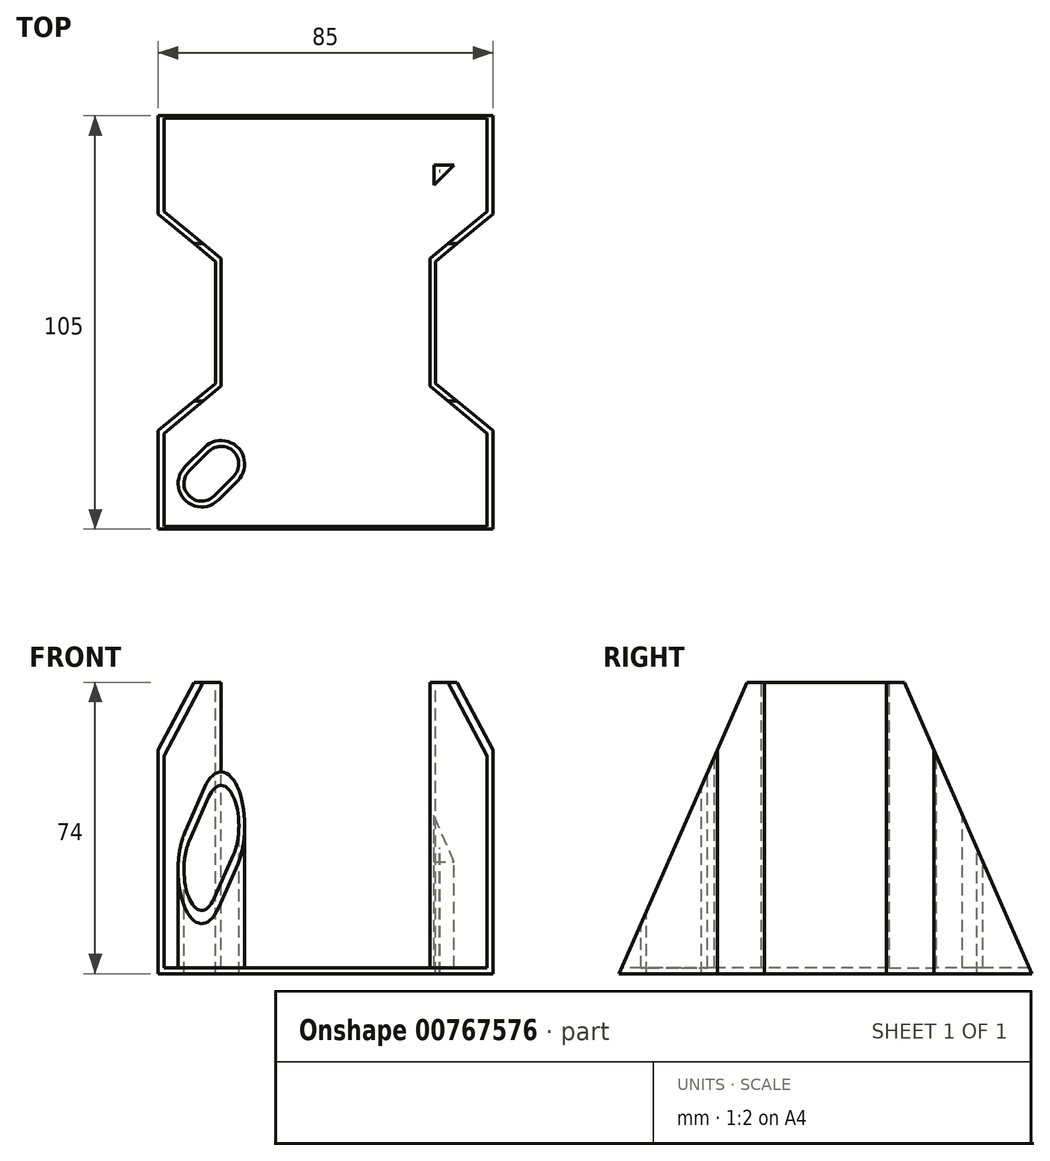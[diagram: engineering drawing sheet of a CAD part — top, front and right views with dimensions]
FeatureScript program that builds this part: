
annotation { "Feature Type Name" : "Feature", "Feature Type Description" : "" }
export const myFeature = defineFeature(function(context is Context, id is Id, definition is map)
    precondition{}
    {
        {
            var Q0;
            Q0=qCreatedBy(makeId("Top.planeOp"),FACE);
            var sketch = newSketch(context, id + "F0", { "sketchPlane" : qUnion([Q0])});
            skLineSegment(sketch, "E0.bottom", {"start": v(42.5, 52.5) * mm, "end": v(-42.5, 52.5) * mm});
            skLineSegment(sketch, "E0.top", {"start": v(42.5, -52.5) * mm, "end": v(-42.5, -52.5) * mm});
            skLineSegment(sketch, "E0.right", {"start": v(-42.5, 52.5) * mm, "end": v(-42.5, 27.5) * mm});
            skPoint(sketch, "E0.middle", {"position": v(0, 0) * mm});
            skLineSegment(sketch, "E1", {"start": v(-28, 15.5) * mm, "end": v(-28, -15.5) * mm});
            skLineSegment(sketch, "E2", {"start": v(-28, -15.5) * mm, "end": v(-42.5, -27.5) * mm});
            skLineSegment(sketch, "E3", {"start": v(-28, 15.5) * mm, "end": v(-42.5, 27.5) * mm});
            skLineSegment(sketch, "E4.trimOffspring", {"start": v(-42.5, -27.5) * mm, "end": v(-42.5, -52.5) * mm});
            skLineSegment(sketch, "E5.MirrorCS", {"start": v(42.5, 52.5) * mm, "end": v(42.5, 27.5) * mm});
            skLineSegment(sketch, "E6.MirrorCS", {"start": v(28, 15.5) * mm, "end": v(42.5, 27.5) * mm});
            skLineSegment(sketch, "E7.MirrorCS", {"start": v(28, 15.5) * mm, "end": v(28, -15.5) * mm});
            skLineSegment(sketch, "E8.MirrorCS", {"start": v(28, -15.5) * mm, "end": v(42.5, -27.5) * mm});
            skLineSegment(sketch, "E9.MirrorCS", {"start": v(42.5, -27.5) * mm, "end": v(42.5, -52.5) * mm});
            skLineSegment(sketch, "E10", {"start": v(31.48, 40.92) * mm, "end": v(26.53, 35.97) * mm});
            skLineSegment(sketch, "E11", {"start": v(29, 49.2) * mm, "end": v(29, 5.37) * mm});
            skLineSegment(sketch, "E12", {"start": v(18.9, 38.5) * mm, "end": v(37.9, 38.5) * mm});
            skArc(sketch, "E13.0.startCap", {"start": v(28.3, 44.1) * mm, "mid": v(34.66, 44.1) * mm, "end": v(34.66, 37.74) * mm});
            skArc(sketch, "E13.0.endCap", {"start": v(29.71, 32.8) * mm, "mid": v(23.35, 32.8) * mm, "end": v(23.35, 39.16) * mm});
            skLineSegment(sketch, "E13.0.left", {"start": v(34.66, 37.74) * mm, "end": v(29.71, 32.8) * mm});
            skLineSegment(sketch, "E13.0.right", {"start": v(28.3, 44.1) * mm, "end": v(23.35, 39.16) * mm});
            skLineSegment(sketch, "E14.MirrorCS", {"start": v(-28.3, 44.1) * mm, "end": v(-23.35, 39.16) * mm});
            skArc(sketch, "E15.MirrorCS", {"start": v(-28.3, 44.1) * mm, "mid": v(-34.66, 44.1) * mm, "end": v(-34.66, 37.74) * mm});
            skLineSegment(sketch, "E16.MirrorCS", {"start": v(-34.66, 37.74) * mm, "end": v(-29.71, 32.8) * mm});
            skArc(sketch, "E17.MirrorCS", {"start": v(-29.71, 32.8) * mm, "mid": v(-23.35, 32.8) * mm, "end": v(-23.35, 39.16) * mm});
            skArc(sketch, "E18.MirrorCS", {"start": v(-29.71, -32.8) * mm, "mid": v(-23.35, -32.8) * mm, "end": v(-23.35, -39.16) * mm});
            skLineSegment(sketch, "E19.MirrorCS", {"start": v(-28.3, -44.1) * mm, "end": v(-23.35, -39.16) * mm});
            skArc(sketch, "E20.MirrorCS", {"start": v(-28.3, -44.1) * mm, "mid": v(-34.66, -44.1) * mm, "end": v(-34.66, -37.74) * mm});
            skLineSegment(sketch, "E21.MirrorCS", {"start": v(-34.66, -37.74) * mm, "end": v(-29.71, -32.8) * mm});
            skLineSegment(sketch, "E22.MirrorCS", {"start": v(28.3, -44.1) * mm, "end": v(23.35, -39.16) * mm});
            skArc(sketch, "E23.MirrorCS", {"start": v(28.3, -44.1) * mm, "mid": v(34.66, -44.1) * mm, "end": v(34.66, -37.74) * mm});
            skLineSegment(sketch, "E24.MirrorCS", {"start": v(34.66, -37.74) * mm, "end": v(29.71, -32.8) * mm});
            skArc(sketch, "E25.MirrorCS", {"start": v(29.71, -32.8) * mm, "mid": v(23.35, -32.8) * mm, "end": v(23.35, -39.16) * mm});
            skSolve(sketch);
        }
        {
            var Q0;
            Q0=makeQuery(id+"F0.imprint","IMPRINT",FACE,{"disambiguationData":[TD([[makeQuery(id+"F0.imprint","IMPRINT",EDGE,{"derivedFrom":sQuery(id+"F0.wireOp",EDGE,"E0.bottom")}),1.0]])]});
            var Q1;
            Q1=makeQuery(id+"F0.imprint","IMPRINT",FACE,{"disambiguationData":[TD([[makeQuery(id+"F0.imprint","IMPRINT",EDGE,{"derivedFrom":sQuery(id+"F0.wireOp",EDGE,"E22.MirrorCS")}),-1.0]])]});
            var Q2;
            Q2=makeQuery(id+"F0.imprint","IMPRINT",FACE,{"disambiguationData":[TD([[makeQuery(id+"F0.imprint","IMPRINT",EDGE,{"derivedFrom":sQuery(id+"F0.wireOp",EDGE,"E14.MirrorCS")}),-1.0]])]});
            var Q3;
            Q3=makeQuery(id+"F0.imprint","IMPRINT",FACE,{"disambiguationData":[TD([[makeQuery(id+"F0.imprint","IMPRINT",EDGE,{"derivedFrom":sQuery(id+"F0.wireOp",EDGE,"E18.MirrorCS")}),-1.0]])]});
            var Q4;
            {var subQ0=sQuery(id+"F0.wireOp",EDGE,"E13.0.left");Q4=makeQuery(id+"F0.imprint","IMPRINT",FACE,{"disambiguationData":[TD([[makeQuery(id+"F0.imprint","IMPRINT",EDGE,{"derivedFrom":subQ0}),-1.0]])]});}
            var Q5;
            {var subQ0=sQuery(id+"F0.wireOp",EDGE,"E11");var subQ1=makeQuery(id+"F0.imprint","INTERSECT",VERTEX,{"derivedFrom":[sQuery(id+"F0.wireOp",EDGE,"E10"),subQ0]});Q5=makeQuery(id+"F0.imprint","IMPRINT",FACE,{"disambiguationData":[TD([[makeQuery(id+"F0.imprint","IMPRINT",EDGE,{"disambiguationData":[TD([[subQ1,1.0]])],"derivedFrom":subQ0}),-1.0]])]});}
            var Q6;
            {var subQ0=sQuery(id+"F0.wireOp",EDGE,"E13.0.startCap");var subQ1=sQuery(id+"F0.wireOp",EDGE,"E11");var subQ2=makeQuery(id+"F0.imprint","INTERSECT",VERTEX,{"derivedFrom":[subQ1,subQ0]});Q6=makeQuery(id+"F0.imprint","IMPRINT",FACE,{"disambiguationData":[TD([[makeQuery(id+"F0.imprint","IMPRINT",EDGE,{"disambiguationData":[TD([[subQ2,-1.0]])],"derivedFrom":subQ1}),1.0]])]});}
            var Q7;
            {var subQ0=sQuery(id+"F0.wireOp",EDGE,"E13.0.right");Q7=makeQuery(id+"F0.imprint","IMPRINT",FACE,{"disambiguationData":[TD([[makeQuery(id+"F0.imprint","IMPRINT",EDGE,{"derivedFrom":subQ0}),1.0]])]});}
            extrude(context, id + "F1", {"entities" : qUnion([Q0, Q1, Q2, Q3, Q4, Q5, Q6, Q7]), "oppositeDirection" : true, "depth" : 74 * mm, "offsetDistance" : 25 * mm});
        }
        {
            var Q0;
            Q0=qCreatedBy(makeId("Right.planeOp"),FACE);
            var sketch = newSketch(context, id + "F2", { "sketchPlane" : qUnion([Q0])});
            skLineSegment(sketch, "E26", {"start": v(-52.5, -74) * mm, "end": v(-20, 0) * mm});
            skLineSegment(sketch, "E27", {"start": v(-20, 0) * mm, "end": v(20, 0) * mm});
            skLineSegment(sketch, "E28", {"start": v(20, 0) * mm, "end": v(52.5, -74) * mm});
            skLineSegment(sketch, "E29", {"start": v(-52.5, 0) * mm, "end": v(-52.5, -74) * mm});
            skLineSegment(sketch, "E30", {"start": v(-52.5, 0) * mm, "end": v(52.9, 0) * mm});
            skLineSegment(sketch, "E31", {"start": v(52.9, 0) * mm, "end": v(52.5, -74) * mm});
            skSolve(sketch);
        }
        {
            var Q0;
            Q0 = qSketchRegion(id + "F2", true);
            extrude(context, id + "F3", {"entities" : qUnion([Q0]), "operationType" : NewBodyOperationType.REMOVE, "endBound" : BoundingType.SYMMETRIC, "oppositeDirection" : true, "depth" : 100 * mm, "offsetDistance" : 25 * mm});
        }
        {
            var Q0;
            Q0=makeQuery(id+"F1.opExtrude","CAP_FACE",FACE,{"disambiguationData":[OSD([sQuery(id+"F0.wireOp",EDGE,"E0.bottom"),sQuery(id+"F0.wireOp",EDGE,"E0.top"),sQuery(id+"F0.wireOp",EDGE,"E0.right"),sQuery(id+"F0.wireOp",EDGE,"E1"),sQuery(id+"F0.wireOp",EDGE,"E2"),sQuery(id+"F0.wireOp",EDGE,"E3"),sQuery(id+"F0.wireOp",EDGE,"E4.trimOffspring"),sQuery(id+"F0.wireOp",EDGE,"E5.MirrorCS"),sQuery(id+"F0.wireOp",EDGE,"E6.MirrorCS"),sQuery(id+"F0.wireOp",EDGE,"E7.MirrorCS"),sQuery(id+"F0.wireOp",EDGE,"E8.MirrorCS"),sQuery(id+"F0.wireOp",EDGE,"E9.MirrorCS"),sQuery(id+"F0.wireOp",EDGE,"E13.0.startCap"),sQuery(id+"F0.wireOp",EDGE,"E13.0.endCap"),sQuery(id+"F0.wireOp",EDGE,"E13.0.left"),sQuery(id+"F0.wireOp",EDGE,"E13.0.right"),sQuery(id+"F0.wireOp",EDGE,"E14.MirrorCS"),sQuery(id+"F0.wireOp",EDGE,"E15.MirrorCS"),sQuery(id+"F0.wireOp",EDGE,"E16.MirrorCS"),sQuery(id+"F0.wireOp",EDGE,"E17.MirrorCS"),sQuery(id+"F0.wireOp",EDGE,"E18.MirrorCS"),sQuery(id+"F0.wireOp",EDGE,"E19.MirrorCS"),sQuery(id+"F0.wireOp",EDGE,"E20.MirrorCS"),sQuery(id+"F0.wireOp",EDGE,"E21.MirrorCS"),sQuery(id+"F0.wireOp",EDGE,"E22.MirrorCS"),sQuery(id+"F0.wireOp",EDGE,"E23.MirrorCS"),sQuery(id+"F0.wireOp",EDGE,"E24.MirrorCS"),sQuery(id+"F0.wireOp",EDGE,"E25.MirrorCS")])],"isStart":true});
            var Q1;
            Q1=makeQuery(id+"F3.boolean.opBoolean","COPY",FACE,{"derivedFrom":makeQuery(id+"F3.opExtrude","SWEPT_FACE",FACE,{"disambiguationData":[OSD([sQuery(id+"F2.wireOp",EDGE,"E26")])]})});
            var Q2;
            Q2=makeQuery(id+"F3.boolean.opBoolean","COPY",FACE,{"derivedFrom":makeQuery(id+"F3.opExtrude","SWEPT_FACE",FACE,{"disambiguationData":[OSD([sQuery(id+"F2.wireOp",EDGE,"E28")])]})});
            shell(context, id + "F4", {"entities" : qUnion([Q0, Q1, Q2]), "thickness" : 1.5 * mm});
        }
    });
